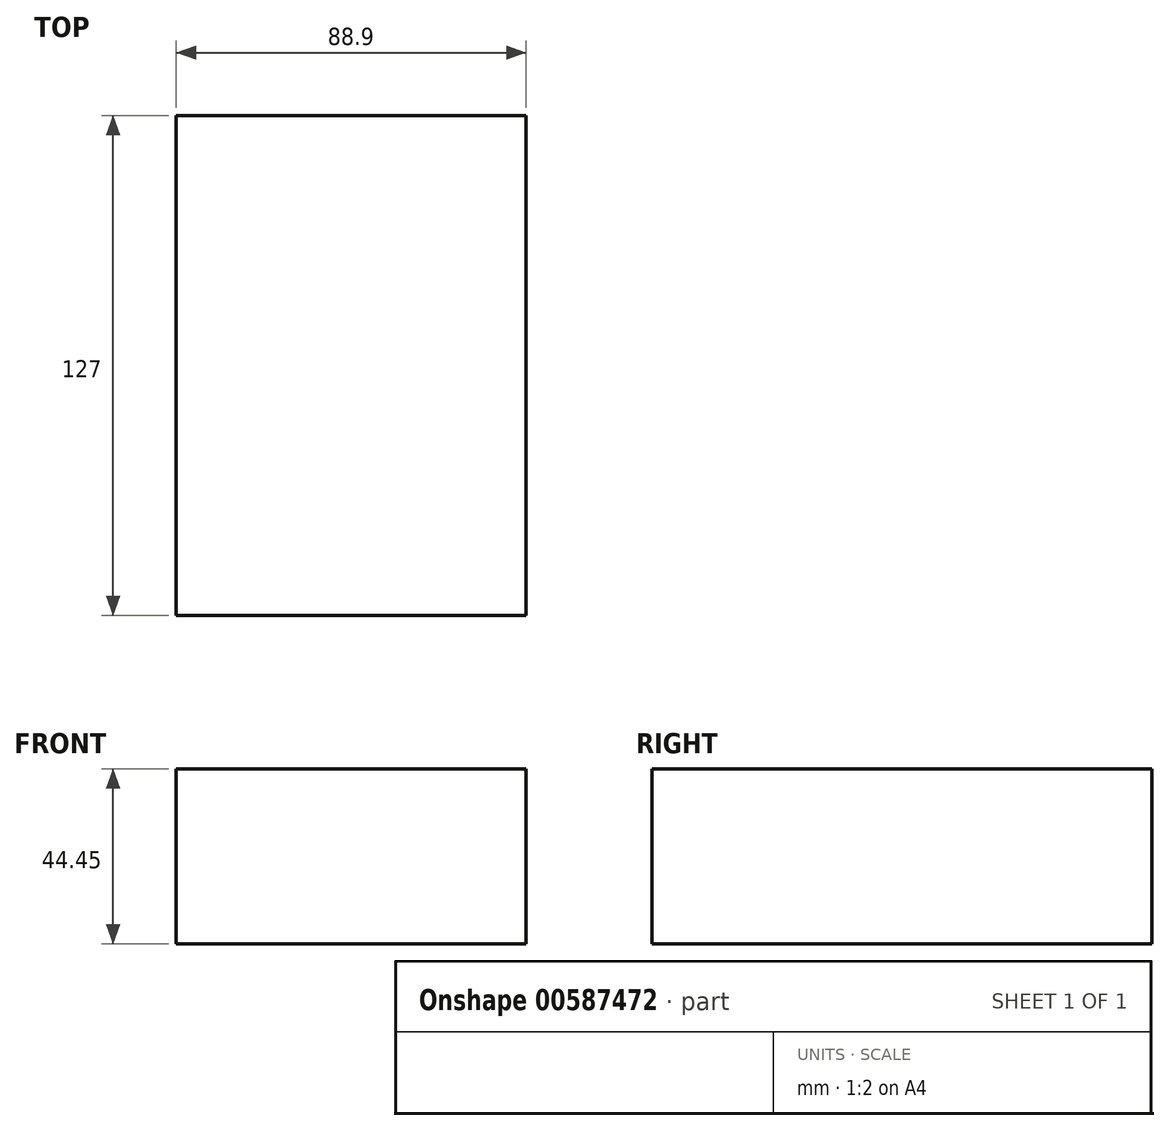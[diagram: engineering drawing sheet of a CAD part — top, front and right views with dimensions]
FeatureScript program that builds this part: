
annotation { "Feature Type Name" : "Feature", "Feature Type Description" : "" }
export const myFeature = defineFeature(function(context is Context, id is Id, definition is map)
    precondition{}
    {
        {
            var Q0;
            Q0=qCreatedBy(makeId("Top.planeOp"),FACE);
            var sketch = newSketch(context, id + "F0", { "sketchPlane" : qUnion([Q0])});
            skLineSegment(sketch, "E0.bottom", {"start": v(0, 37.61) * mm, "end": v(88.9, 37.61) * mm});
            skLineSegment(sketch, "E0.top", {"start": v(0, -89.39) * mm, "end": v(88.9, -89.39) * mm});
            skLineSegment(sketch, "E0.left", {"start": v(0, 37.61) * mm, "end": v(0, -89.39) * mm});
            skLineSegment(sketch, "E0.right", {"start": v(88.9, 37.61) * mm, "end": v(88.9, -89.39) * mm});
            skSolve(sketch);
        }
        {
            var Q0;
            Q0=makeQuery(id+"F0.imprint","IMPRINT",FACE,{"disambiguationData":[TD([[makeQuery(id+"F0.imprint","IMPRINT",EDGE,{"derivedFrom":sQuery(id+"F0.wireOp",EDGE,"E0.bottom")}),-1.0]])]});
            extrude(context, id + "F1", {"entities" : qUnion([Q0]), "depth" : 44.45 * mm, "offsetDistance" : 25.4 * mm});
        }
        {
            var Q0;
            Q0=makeQuery(id+"F1.opExtrude","CAP_FACE",FACE,{"disambiguationData":[OSD([sQuery(id+"F0.wireOp",EDGE,"E0.bottom"),sQuery(id+"F0.wireOp",EDGE,"E0.top"),sQuery(id+"F0.wireOp",EDGE,"E0.left"),sQuery(id+"F0.wireOp",EDGE,"E0.right")])],"isStart":false});
            var sketch = newSketch(context, id + "F2", { "sketchPlane" : qUnion([Q0])});
            skLineSegment(sketch, "E1", {"start": v(0, -89.39) * mm, "end": v(25.4, -89.39) * mm});
            skSolve(sketch);
        }
        {
            var Q0;
            {var subQ2=sQuery(id+"F2.wireOp",EDGE,"E1");Q0=makeQuery(id+"F2.imprint","IMPRINT",FACE,{"disambiguationData":[TD([[makeQuery(id+"F2.imprint","IMPRINT",EDGE,{"derivedFrom":subQ2}),1.0]])]});}
            var sketch = newSketch(context, id + "F3", { "sketchPlane" : qUnion([Q0])});
            skLineSegment(sketch, "E2", {"start": v(25.38, -89.7) * mm, "end": v(25.38, 11.9) * mm});
            skLineSegment(sketch, "E3", {"start": v(25.38, 11.9) * mm, "end": v(0, 37.46) * mm});
            skLineSegment(sketch, "E4", {"start": v(63.64, -89.7) * mm, "end": v(63.64, 11.9) * mm});
            skLineSegment(sketch, "E5", {"start": v(63.64, 11.9) * mm, "end": v(88.4, 37.23) * mm});
            skSolve(sketch);
        }
        {
            var Q0;
            {var subQ2=sQuery(id+"F2.wireOp",EDGE,"E1");Q0=makeQuery(id+"F2.imprint","IMPRINT",FACE,{"disambiguationData":[TD([[makeQuery(id+"F2.imprint","IMPRINT",EDGE,{"derivedFrom":subQ2}),1.0]])]});}
            var Q1;
            {var subQ5=sQuery(id+"F3.wireOp",EDGE,"E3");Q1=makeQuery(id+"F3.imprint","IMPRINT",FACE,{"disambiguationData":[TD([[makeQuery(id+"F3.imprint","IMPRINT",EDGE,{"derivedFrom":subQ5}),-1.0]])]});}
            extrude(context, id + "F4", {"entities" : qUnion([Q0, Q1]), "operationType" : NewBodyOperationType.ADD, "oppositeDirection" : true, "depth" : 42.93 * mm, "offsetDistance" : 25.4 * mm});
        }
    });
